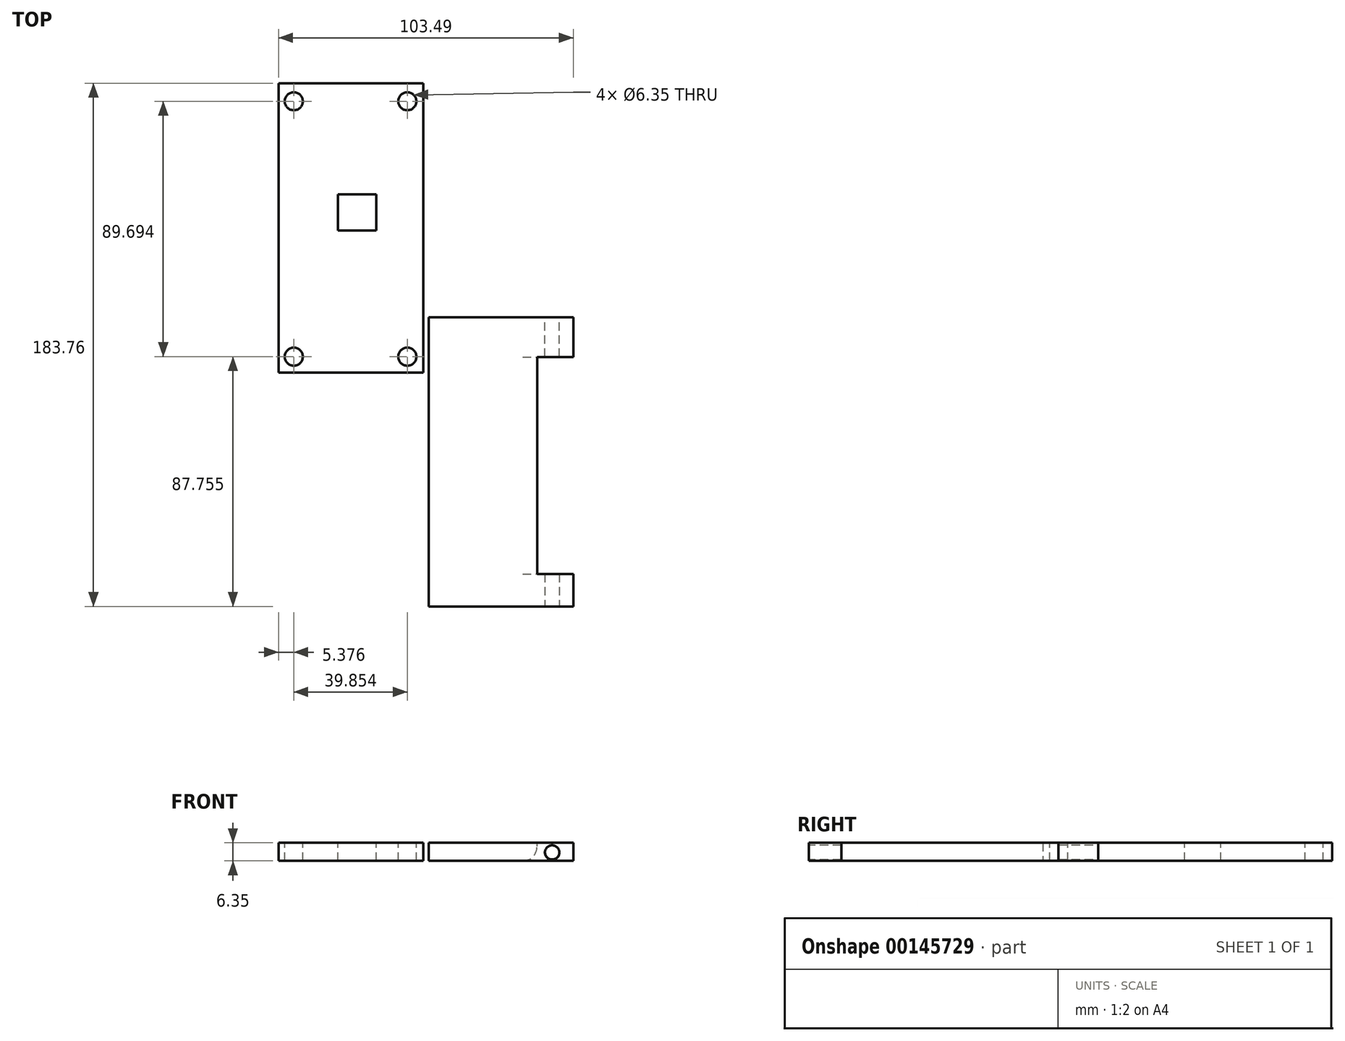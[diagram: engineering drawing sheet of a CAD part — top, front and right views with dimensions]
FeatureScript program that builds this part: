
annotation { "Feature Type Name" : "Feature", "Feature Type Description" : "" }
export const myFeature = defineFeature(function(context is Context, id is Id, definition is map)
    precondition{}
    {
        {
            var Q0;
            Q0=qCreatedBy(makeId("Top.planeOp"),FACE);
            var sketch = newSketch(context, id + "F0", { "sketchPlane" : qUnion([Q0])});
            skLineSegment(sketch, "E0.bottom", {"start": v(-27.55, 78.78) * mm, "end": v(23.25, 78.78) * mm});
            skLineSegment(sketch, "E0.top", {"start": v(-27.55, -22.82) * mm, "end": v(23.25, -22.82) * mm});
            skLineSegment(sketch, "E0.left", {"start": v(-27.55, 78.78) * mm, "end": v(-27.55, -22.82) * mm});
            skLineSegment(sketch, "E0.right", {"start": v(23.25, 78.78) * mm, "end": v(23.25, -22.82) * mm});
            skSolve(sketch);
        }
        {
            var Q0;
            Q0=makeQuery(id+"F0.imprint","IMPRINT",FACE,{"disambiguationData":[TD([[makeQuery(id+"F0.imprint","IMPRINT",EDGE,{"derivedFrom":sQuery(id+"F0.wireOp",EDGE,"E0.bottom")}),-1.0]])]});
            extrude(context, id + "F1", {"entities" : qUnion([Q0]), "depth" : 6.35 * mm});
        }
        {
            var Q0;
            Q0=makeQuery(id+"F1.opExtrude","CAP_FACE",FACE,{"disambiguationData":[OSD([sQuery(id+"F0.wireOp",EDGE,"E0.bottom"),sQuery(id+"F0.wireOp",EDGE,"E0.top"),sQuery(id+"F0.wireOp",EDGE,"E0.left"),sQuery(id+"F0.wireOp",EDGE,"E0.right")])],"isStart":false});
            var sketch = newSketch(context, id + "F2", { "sketchPlane" : qUnion([Q0])});
            skSolve(sketch);
        }
        {
            var Q0;
            Q0=makeQuery(id+"F2.imprint","IMPRINT",FACE,{"disambiguationData":[TD([[makeQuery(id+"F2.imprint","IMPRINT",EDGE,{"derivedFrom":makeQuery(id+"F1.opExtrude","CAP_EDGE",EDGE,{"disambiguationData":[OSD([sQuery(id+"F0.wireOp",EDGE,"E0.bottom")])],"isStart":false})}),-1.0]])]});
            var sketch = newSketch(context, id + "F3", { "sketchPlane" : qUnion([Q0])});
            skCircle(sketch, "E1", {"center": v(-22.17, 72.47) * mm, "radius": 3.18 * mm});
            skCircle(sketch, "E2", {"center": v(-22.17, -17.23) * mm, "radius": 3.18 * mm});
            skLineSegment(sketch, "E3", {"start": v(-22.17, 72.47) * mm, "end": v(-22.17, -17.23) * mm, "construction": true});
            skLineSegment(sketch, "E4", {"start": v(-27.5, 30.2) * mm, "end": v(73.73, 30.2) * mm});
            skCircle(sketch, "E5", {"center": v(17.68, 72.47) * mm, "radius": 3.18 * mm});
            skCircle(sketch, "E6", {"center": v(17.68, -17.23) * mm, "radius": 3.18 * mm});
            skLineSegment(sketch, "E7", {"start": v(-22.17, 72.47) * mm, "end": v(17.68, 72.47) * mm, "construction": true});
            skLineSegment(sketch, "E8", {"start": v(17.68, 72.47) * mm, "end": v(17.68, -17.23) * mm, "construction": true});
            skLineSegment(sketch, "E9", {"start": v(17.68, -17.23) * mm, "end": v(-22.17, -17.23) * mm, "construction": true});
            skSolve(sketch);
        }
        {
            var Q0;
            Q0 = qSketchRegion(id + "F3", true);
            extrude(context, id + "F4", {"entities" : qUnion([Q0]), "operationType" : NewBodyOperationType.REMOVE, "oppositeDirection" : true, "depth" : 25.4 * mm});
        }
        {
            var Q0;
            Q0=makeQuery(id+"F2.imprint","IMPRINT",FACE,{"disambiguationData":[TD([[makeQuery(id+"F2.imprint","IMPRINT",EDGE,{"derivedFrom":makeQuery(id+"F1.opExtrude","CAP_EDGE",EDGE,{"disambiguationData":[OSD([sQuery(id+"F0.wireOp",EDGE,"E0.bottom")])],"isStart":false})}),-1.0]])]});
            var sketch = newSketch(context, id + "F5", { "sketchPlane" : qUnion([Q0])});
            skLineSegment(sketch, "E10.bottom", {"start": v(6.73, 39.72) * mm, "end": v(-6.73, 39.72) * mm});
            skLineSegment(sketch, "E10.top", {"start": v(6.73, 27.02) * mm, "end": v(-6.73, 27.02) * mm});
            skLineSegment(sketch, "E10.left", {"start": v(6.73, 39.72) * mm, "end": v(6.73, 27.02) * mm});
            skLineSegment(sketch, "E10.right", {"start": v(-6.73, 39.72) * mm, "end": v(-6.73, 27.02) * mm});
            skPoint(sketch, "E10.middle", {"position": v(0, 33.37) * mm});
            skSolve(sketch);
        }
        {
            var Q0;
            Q0=makeQuery(id+"F5.imprint","IMPRINT",FACE,{"disambiguationData":[TD([[makeQuery(id+"F5.imprint","IMPRINT",EDGE,{"derivedFrom":sQuery(id+"F5.wireOp",EDGE,"E10.bottom")}),-1.0]])]});
            var sketch = newSketch(context, id + "F6", { "sketchPlane" : qUnion([Q0])});
            skLineSegment(sketch, "E11", {"start": v(22.98, 78.67) * mm, "end": v(22.98, -22.73) * mm});
            skSolve(sketch);
        }
        {
            var Q0;
            Q0=makeQuery(id+"F6.imprint","IMPRINT",FACE,{"disambiguationData":[TD([[makeQuery(id+"F6.imprint","IMPRINT",EDGE,{"derivedFrom":makeQuery(id+"F5.imprint","IMPRINT",EDGE,{"derivedFrom":sQuery(id+"F5.wireOp",EDGE,"E10.bottom")})}),1.0]])]});
            extrude(context, id + "F7", {"entities" : qUnion([Q0]), "operationType" : NewBodyOperationType.REMOVE, "oppositeDirection" : true, "depth" : 25.4 * mm});
        }
        {
            var Q0;
            Q0=qCreatedBy(makeId("Top.planeOp"),FACE);
            var sketch = newSketch(context, id + "F8", { "sketchPlane" : qUnion([Q0])});
            skLineSegment(sketch, "E12.bottom", {"start": v(75.94, -3.38) * mm, "end": v(25.14, -3.38) * mm});
            skLineSegment(sketch, "E12.top", {"start": v(75.94, -104.98) * mm, "end": v(25.14, -104.98) * mm});
            skLineSegment(sketch, "E12.left", {"start": v(75.94, -3.38) * mm, "end": v(75.94, -104.98) * mm});
            skLineSegment(sketch, "E12.right", {"start": v(25.14, -3.38) * mm, "end": v(25.14, -104.98) * mm});
            skPoint(sketch, "E12.middle", {"position": v(50.54, -54.18) * mm});
            skSolve(sketch);
        }
        {
            var Q0;
            Q0=makeQuery(id+"F8.imprint","IMPRINT",FACE,{"disambiguationData":[TD([[makeQuery(id+"F8.imprint","IMPRINT",EDGE,{"derivedFrom":sQuery(id+"F8.wireOp",EDGE,"E12.bottom")}),1.0]])]});
            extrude(context, id + "F9", {"entities" : qUnion([Q0]), "depth" : 6.35 * mm});
        }
        {
            var Q0;
            Q0=makeQuery(id+"F9.opExtrude","CAP_FACE",FACE,{"disambiguationData":[OSD([sQuery(id+"F8.wireOp",EDGE,"E12.bottom"),sQuery(id+"F8.wireOp",EDGE,"E12.top"),sQuery(id+"F8.wireOp",EDGE,"E12.left"),sQuery(id+"F8.wireOp",EDGE,"E12.right")])],"isStart":false});
            var sketch = newSketch(context, id + "F10", { "sketchPlane" : qUnion([Q0])});
            skLineSegment(sketch, "E13.bottom", {"start": v(63.24, -17.32) * mm, "end": v(75.94, -17.32) * mm});
            skLineSegment(sketch, "E13.top", {"start": v(63.24, -93.52) * mm, "end": v(75.94, -93.52) * mm});
            skLineSegment(sketch, "E13.left", {"start": v(63.24, -17.32) * mm, "end": v(63.24, -93.52) * mm});
            skLineSegment(sketch, "E13.right", {"start": v(75.94, -17.32) * mm, "end": v(75.94, -93.52) * mm});
            skSolve(sketch);
        }
        {
            var Q0;
            Q0=makeQuery(id+"F10.imprint","IMPRINT",FACE,{"disambiguationData":[TD([[makeQuery(id+"F10.imprint","IMPRINT",EDGE,{"derivedFrom":sQuery(id+"F10.wireOp",EDGE,"E13.bottom")}),-1.0]])]});
            extrude(context, id + "F11", {"entities" : qUnion([Q0]), "operationType" : NewBodyOperationType.REMOVE, "oppositeDirection" : true, "depth" : 25.4 * mm});
        }
        {
            var Q0;
            Q0=makeQuery(id+"F9.opExtrude","SWEPT_FACE",FACE,{"disambiguationData":[OSD([sQuery(id+"F8.wireOp",EDGE,"E12.top")])]});
            var sketch = newSketch(context, id + "F12", { "sketchPlane" : qUnion([Q0])});
            skCircle(sketch, "E14", {"center": v(68.53, 2.94) * mm, "radius": 2.54 * mm});
            skSolve(sketch);
        }
        {
            var Q0;
            Q0=makeQuery(id+"F12.imprint","IMPRINT",FACE,{"disambiguationData":[TD([[makeQuery(id+"F12.imprint","IMPRINT",EDGE,{"derivedFrom":sQuery(id+"F12.wireOp",EDGE,"E14")}),1.0]])]});
            extrude(context, id + "F13", {"entities" : qUnion([Q0]), "operationType" : NewBodyOperationType.REMOVE, "oppositeDirection" : true, "depth" : 25.4 * mm});
        }
        {
            var Q0;
            Q0=makeQuery(id+"F9.opExtrude","SWEPT_FACE",FACE,{"disambiguationData":[OSD([sQuery(id+"F8.wireOp",EDGE,"E12.bottom")])]});
            var sketch = newSketch(context, id + "F14", { "sketchPlane" : qUnion([Q0])});
            skCircle(sketch, "E15", {"center": v(-68.56, 3.04) * mm, "radius": 2.54 * mm});
            skSolve(sketch);
        }
        {
            var Q0;
            Q0=makeQuery(id+"F14.imprint","IMPRINT",FACE,{"disambiguationData":[TD([[makeQuery(id+"F14.imprint","IMPRINT",EDGE,{"derivedFrom":sQuery(id+"F14.wireOp",EDGE,"E15")}),1.0]])]});
            extrude(context, id + "F15", {"entities" : qUnion([Q0]), "operationType" : NewBodyOperationType.REMOVE, "oppositeDirection" : true, "depth" : 25.4 * mm});
        }
        {
            var Q0;
            Q0=makeQuery(id+"F11.boolean.opBoolean","INTERSECT",EDGE,{"derivedFrom":[makeQuery(id+"F9.opExtrude","CAP_FACE",FACE,{"disambiguationData":[OSD([sQuery(id+"F8.wireOp",EDGE,"E12.bottom"),sQuery(id+"F8.wireOp",EDGE,"E12.top"),sQuery(id+"F8.wireOp",EDGE,"E12.left"),sQuery(id+"F8.wireOp",EDGE,"E12.right")])],"isStart":true}),makeQuery(id+"F11.opExtrude","SWEPT_FACE",FACE,{"disambiguationData":[OSD([sQuery(id+"F10.wireOp",EDGE,"E13.left")])]})]});
            fillet(context, id + "F16", {"entities" : qUnion([Q0]), "radius" : 5.08 * mm, "tangentPropagation" : true, "allowEdgeOverflow" : false});
        }
    });
